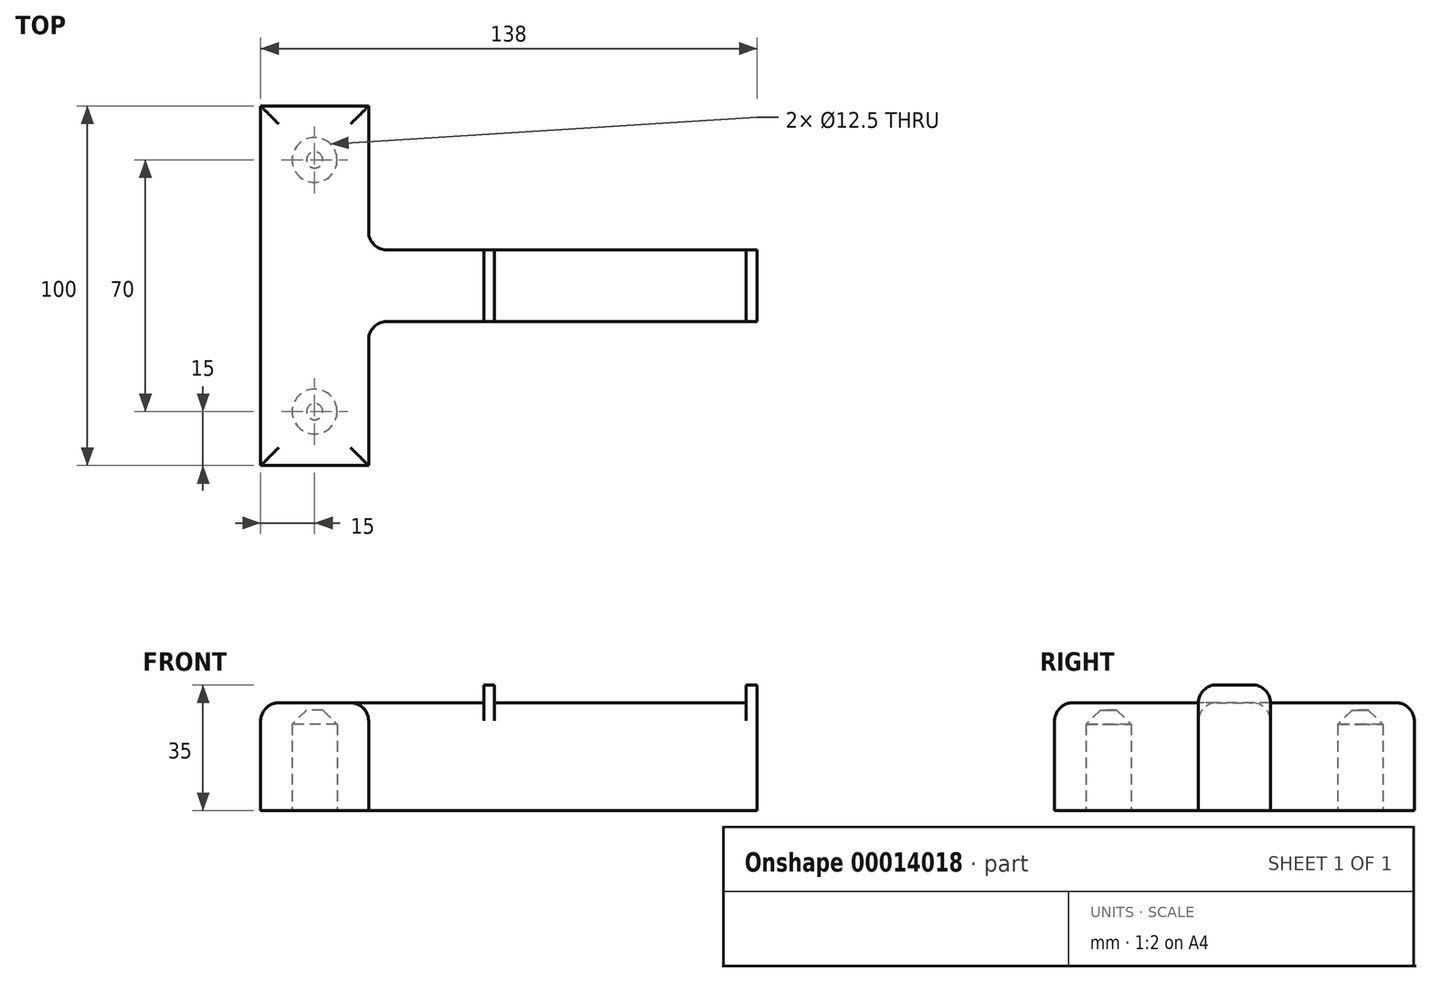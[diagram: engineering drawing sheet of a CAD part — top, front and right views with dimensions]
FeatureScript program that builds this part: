
annotation { "Feature Type Name" : "Feature", "Feature Type Description" : "" }
export const myFeature = defineFeature(function(context is Context, id is Id, definition is map)
    precondition{}
    {
        {
            var Q0;
            Q0=qCreatedBy(makeId("Top.planeOp"),FACE);
            var sketch = newSketch(context, id + "F0", { "sketchPlane" : qUnion([Q0])});
            skCircle(sketch, "E0", {"center": v(0, -35) * mm, "radius": 6.25 * mm});
            skCircle(sketch, "E1", {"center": v(0, 35) * mm, "radius": 6.25 * mm});
            skLineSegment(sketch, "E2.rect.bottom", {"start": v(15, 50) * mm, "end": v(-15, 50) * mm});
            skLineSegment(sketch, "E2.rect.top", {"start": v(15, -50) * mm, "end": v(-15, -50) * mm});
            skLineSegment(sketch, "E2.rect.left", {"start": v(15, 50) * mm, "end": v(15, -50) * mm});
            skLineSegment(sketch, "E2.rect.right", {"start": v(-15, 50) * mm, "end": v(-15, -50) * mm});
            skPoint(sketch, "E2.rect.middle", {"position": v(0, 0) * mm});
            skLineSegment(sketch, "E3.bottom", {"start": v(0, -10) * mm, "end": v(120, -10) * mm});
            skLineSegment(sketch, "E3.top", {"start": v(0, 10) * mm, "end": v(120, 10) * mm});
            skLineSegment(sketch, "E3.left", {"start": v(0, -10) * mm, "end": v(0, 10) * mm});
            skLineSegment(sketch, "E3.right", {"start": v(120, -10) * mm, "end": v(120, 10) * mm});
            skLineSegment(sketch, "E4", {"start": v(120, -10) * mm, "end": v(123, -10) * mm});
            skLineSegment(sketch, "E5", {"start": v(123, -10) * mm, "end": v(123, 10) * mm});
            skLineSegment(sketch, "E6", {"start": v(123, 10) * mm, "end": v(120, 10) * mm});
            skLineSegment(sketch, "E7", {"start": v(50, 10) * mm, "end": v(50, -10) * mm});
            skLineSegment(sketch, "E8", {"start": v(47, 10) * mm, "end": v(47, -10) * mm});
            skSolve(sketch);
        }
        {
            var Q0;
            Q0=makeQuery(id+"F0.imprint","IMPRINT",FACE,{"disambiguationData":[TD([[makeQuery(id+"F0.imprint","IMPRINT",EDGE,{"derivedFrom":sQuery(id+"F0.wireOp",EDGE,"E0")}),-1.0]])]});
            var Q1;
            {var subQ0=sQuery(id+"F0.wireOp",EDGE,"E3.left");Q1=makeQuery(id+"F0.imprint","IMPRINT",FACE,{"disambiguationData":[TD([[makeQuery(id+"F0.imprint","IMPRINT",EDGE,{"derivedFrom":subQ0}),-1.0]])]});}
            var Q2;
            {var subQ0=sQuery(id+"F0.wireOp",EDGE,"E3.right");Q2=makeQuery(id+"F0.imprint","IMPRINT",FACE,{"disambiguationData":[TD([[makeQuery(id+"F0.imprint","IMPRINT",EDGE,{"derivedFrom":subQ0}),1.0]])]});}
            var Q3;
            Q3=makeQuery(id+"F0.imprint","IMPRINT",FACE,{"disambiguationData":[TD([[makeQuery(id+"F0.imprint","IMPRINT",EDGE,{"derivedFrom":sQuery(id+"F0.wireOp",EDGE,"E0")}),1.0]])]});
            var Q4;
            Q4=makeQuery(id+"F0.imprint","IMPRINT",FACE,{"disambiguationData":[TD([[makeQuery(id+"F0.imprint","IMPRINT",EDGE,{"derivedFrom":sQuery(id+"F0.wireOp",EDGE,"E1")}),1.0]])]});
            var Q5;
            {var subQ3=sQuery(id+"F0.wireOp",EDGE,"E8");Q5=makeQuery(id+"F0.imprint","IMPRINT",FACE,{"disambiguationData":[TD([[makeQuery(id+"F0.imprint","IMPRINT",EDGE,{"derivedFrom":subQ3}),-1.0]])]});}
            var Q6;
            {var subQ1=sQuery(id+"F0.wireOp",EDGE,"E7");Q6=makeQuery(id+"F0.imprint","IMPRINT",FACE,{"disambiguationData":[TD([[makeQuery(id+"F0.imprint","IMPRINT",EDGE,{"derivedFrom":subQ1}),-1.0]])]});}
            extrude(context, id + "F1", {"entities" : qUnion([Q0, Q1, Q2, Q3, Q4, Q5, Q6]), "depth" : 30 * mm});
        }
        {
            var Q0;
            Q0=makeQuery(id+"F0.imprint","IMPRINT",FACE,{"disambiguationData":[TD([[makeQuery(id+"F0.imprint","IMPRINT",EDGE,{"derivedFrom":sQuery(id+"F0.wireOp",EDGE,"E3.right")}),-1.0]])]});
            var Q1;
            {var subQ1=sQuery(id+"F0.wireOp",EDGE,"E7");Q1=makeQuery(id+"F0.imprint","IMPRINT",FACE,{"disambiguationData":[TD([[makeQuery(id+"F0.imprint","IMPRINT",EDGE,{"derivedFrom":subQ1}),-1.0]])]});}
            extrude(context, id + "F2", {"entities" : qUnion([Q0, Q1]), "operationType" : NewBodyOperationType.ADD, "depth" : 35 * mm});
        }
        {
            var Q0;
            Q0=makeQuery(id+"F0.imprint","IMPRINT",FACE,{"disambiguationData":[TD([[makeQuery(id+"F0.imprint","IMPRINT",EDGE,{"derivedFrom":sQuery(id+"F0.wireOp",EDGE,"E0")}),1.0]])]});
            var Q1;
            Q1=makeQuery(id+"F0.imprint","IMPRINT",FACE,{"disambiguationData":[TD([[makeQuery(id+"F0.imprint","IMPRINT",EDGE,{"derivedFrom":sQuery(id+"F0.wireOp",EDGE,"E1")}),1.0]])]});
            extrude(context, id + "F3", {"entities" : qUnion([Q0, Q1]), "operationType" : NewBodyOperationType.REMOVE, "depth" : 28 * mm});
        }
        {
            var Q0;
            Q0=makeQuery(id+"F3.boolean.opBoolean","COPY",EDGE,{"derivedFrom":makeQuery(id+"F3.opExtrude","CAP_EDGE",EDGE,{"disambiguationData":[OSD([sQuery(id+"F0.wireOp",EDGE,"E0")])],"isStart":false})});
            var Q1;
            Q1=makeQuery(id+"F3.boolean.opBoolean","COPY",EDGE,{"derivedFrom":makeQuery(id+"F3.opExtrude","CAP_EDGE",EDGE,{"disambiguationData":[OSD([sQuery(id+"F0.wireOp",EDGE,"E1")])],"isStart":false})});
            chamfer(context, id + "F4", {"entities" : qUnion([Q0, Q1]), "width" : 4 * mm, "tangentPropagation" : true});
        }
        {
            var Q0;
            Q0=makeQuery(id+"F1.opExtrude","CAP_EDGE",EDGE,{"disambiguationData":[OSD([sQuery(id+"F0.wireOp",EDGE,"E3.bottom")])],"isStart":false});
            var Q1;
            Q1=makeQuery(id+"F1.opExtrude","CAP_EDGE",EDGE,{"disambiguationData":[OSD([sQuery(id+"F0.wireOp",EDGE,"E3.top")])],"isStart":false});
            var Q2;
            Q2=makeQuery(id+"F2.opExtrude","CAP_EDGE",EDGE,{"disambiguationData":[OSD([sQuery(id+"F0.wireOp",EDGE,"E4")])],"isStart":false});
            var Q3;
            Q3=makeQuery(id+"F2.opExtrude","CAP_EDGE",EDGE,{"disambiguationData":[OSD([sQuery(id+"F0.wireOp",EDGE,"E6")])],"isStart":false});
            var Q4;
            {var subQ0=sQuery(id+"F0.wireOp",EDGE,"E2.rect.left");Q4=makeQuery(id+"F1.opExtrude","CAP_EDGE",EDGE,{"disambiguationData":[OSD([subQ0]),TDD([makeQuery(id+"F0.imprint","IMPRINT",EDGE,{"disambiguationData":[TD([[makeQuery(id+"F0.imprint","INTERSECT",VERTEX,{"derivedFrom":[sQuery(id+"F0.wireOp",EDGE,"E2.rect.top"),subQ0]}),1.0]])],"derivedFrom":subQ0})])],"isStart":false});}
            var Q5;
            {var subQ0=sQuery(id+"F0.wireOp",EDGE,"E2.rect.left");Q5=makeQuery(id+"F1.opExtrude","CAP_EDGE",EDGE,{"disambiguationData":[OSD([subQ0]),TDD([makeQuery(id+"F0.imprint","IMPRINT",EDGE,{"disambiguationData":[TD([[makeQuery(id+"F0.imprint","INTERSECT",VERTEX,{"derivedFrom":[sQuery(id+"F0.wireOp",EDGE,"E2.rect.bottom"),subQ0]}),-1.0]])],"derivedFrom":subQ0})])],"isStart":false});}
            var Q6;
            Q6=makeQuery(id+"F1.opExtrude","CAP_EDGE",EDGE,{"disambiguationData":[OSD([sQuery(id+"F0.wireOp",EDGE,"E2.rect.right")])],"isStart":false});
            var Q7;
            Q7=makeQuery(id+"F1.opExtrude","SWEPT_EDGE",EDGE,{"disambiguationData":[OSD([sQuery(id+"F0.wireOp",EDGE,"E2.rect.left"),sQuery(id+"F0.wireOp",EDGE,"E3.bottom")])]});
            var Q8;
            Q8=makeQuery(id+"F1.opExtrude","SWEPT_EDGE",EDGE,{"disambiguationData":[OSD([sQuery(id+"F0.wireOp",EDGE,"E2.rect.left"),sQuery(id+"F0.wireOp",EDGE,"E3.top")])]});
            var Q9;
            Q9=makeQuery(id+"F1.opExtrude","CAP_EDGE",EDGE,{"disambiguationData":[OSD([sQuery(id+"F0.wireOp",EDGE,"E2.rect.top")])],"isStart":false});
            var Q10;
            Q10=makeQuery(id+"F1.opExtrude","CAP_EDGE",EDGE,{"disambiguationData":[OSD([sQuery(id+"F0.wireOp",EDGE,"E2.rect.bottom")])],"isStart":false});
            var Q11;
            Q11=makeQuery(id+"F2.opExtrude","CAP_EDGE",EDGE,{"disambiguationData":[OSD([sQuery(id+"F0.wireOp",EDGE,"E3.bottom")])],"isStart":false});
            var Q12;
            Q12=makeQuery(id+"F2.opExtrude","CAP_EDGE",EDGE,{"disambiguationData":[OSD([sQuery(id+"F0.wireOp",EDGE,"E3.top")])],"isStart":false});
            fillet(context, id + "F5", {"entities" : qUnion([Q0, Q1, Q2, Q3, Q4, Q5, Q6, Q7, Q8, Q9, Q10, Q11, Q12]), "radius" : 5 * mm, "tangentPropagation" : true, "allowEdgeOverflow" : false});
        }
    });
